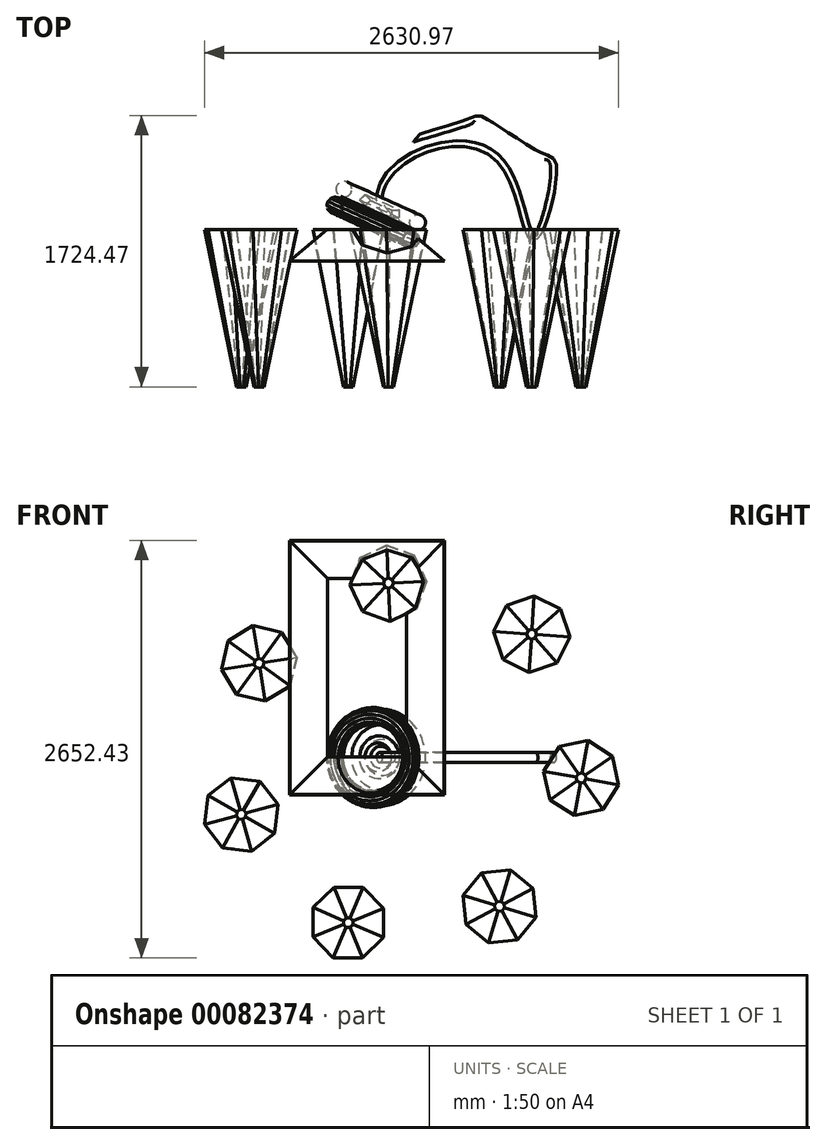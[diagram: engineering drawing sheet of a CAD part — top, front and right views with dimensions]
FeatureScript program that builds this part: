
annotation { "Feature Type Name" : "Feature", "Feature Type Description" : "" }
export const myFeature = defineFeature(function(context is Context, id is Id, definition is map)
    precondition{}
    {
        {
            var Q0;
            Q0=qCreatedBy(makeId("Top.planeOp"),FACE);
            var sketch = newSketch(context, id + "F0", { "sketchPlane" : qUnion([Q0])});
            skLineSegment(sketch, "E0.bottom", {"start": v(-50, 75) * mm, "end": v(-100, 75) * mm});
            skLineSegment(sketch, "E0.top", {"start": v(-50, 125) * mm, "end": v(-100, 125) * mm});
            skLineSegment(sketch, "E0.left", {"start": v(-50, 75) * mm, "end": v(-50, 125) * mm});
            skLineSegment(sketch, "E0.right", {"start": v(-100, 75) * mm, "end": v(-100, 125) * mm});
            skPoint(sketch, "E0.middle", {"position": v(-75, 100) * mm});
            skCircle(sketch, "E1", {"center": v(67, 45) * mm, "radius": 50 * mm});
            skArc(sketch, "E2", {"start": v(-125.25, -15.44) * mm, "mid": v(-116.96, -137.17) * mm, "end": v(-41.75, -41.1) * mm});
            skCircle(sketch, "E3.cCircle", {"center": v(25, -65) * mm, "radius": 52 * mm, "construction": true});
            skLineSegment(sketch, "E3.0", {"start": v(78, -57.37) * mm, "end": v(75.48, -82.88) * mm});
            skLineSegment(sketch, "E3.1", {"start": v(75.48, -82.88) * mm, "end": v(61.4, -104.3) * mm});
            skLineSegment(sketch, "E3.2", {"start": v(61.4, -104.3) * mm, "end": v(38.97, -116.7) * mm});
            skLineSegment(sketch, "E3.3", {"start": v(38.97, -116.7) * mm, "end": v(13.34, -117.27) * mm});
            skLineSegment(sketch, "E3.4", {"start": v(13.34, -117.27) * mm, "end": v(-9.62, -105.86) * mm});
            skLineSegment(sketch, "E3.5", {"start": v(-9.62, -105.86) * mm, "end": v(-24.64, -85.1) * mm});
            skLineSegment(sketch, "E3.6", {"start": v(-24.64, -85.1) * mm, "end": v(-28.3, -59.72) * mm});
            skLineSegment(sketch, "E3.7", {"start": v(-28.3, -59.72) * mm, "end": v(-19.74, -35.56) * mm});
            skLineSegment(sketch, "E3.8", {"start": v(-19.74, -35.56) * mm, "end": v(-0.93, -18.14) * mm});
            skLineSegment(sketch, "E3.9", {"start": v(-0.93, -18.14) * mm, "end": v(23.81, -11.46) * mm});
            skLineSegment(sketch, "E3.10", {"start": v(23.81, -11.46) * mm, "end": v(48.83, -17.04) * mm});
            skLineSegment(sketch, "E3.11", {"start": v(48.83, -17.04) * mm, "end": v(68.4, -33.6) * mm});
            skLineSegment(sketch, "E3.12", {"start": v(68.4, -33.6) * mm, "end": v(78, -57.37) * mm});
            skPoint(sketch, "E3.0.midPoint", {"position": v(76.75, -70.12) * mm});
            skLineSegment(sketch, "E4", {"start": v(-88.57, 324.23) * mm, "end": v(-325.42, -199.43) * mm});
            skSolve(sketch);
        }
        {
            var Q0;
            Q0=makeQuery(id+"F0.imprint","IMPRINT",FACE,{"disambiguationData":[TD([[makeQuery(id+"F0.imprint","IMPRINT",EDGE,{"derivedFrom":sQuery(id+"F0.wireOp",EDGE,"E0.bottom")}),-1.0]])]});
            var Q1;
            Q1=makeQuery(id+"F0.imprint","IMPRINT",FACE,{"disambiguationData":[TD([[makeQuery(id+"F0.imprint","IMPRINT",EDGE,{"derivedFrom":sQuery(id+"F0.wireOp",EDGE,"E1")}),1.0]])]});
            var Q2;
            Q2=makeQuery(id+"F0.imprint","IMPRINT",FACE,{"disambiguationData":[TD([[makeQuery(id+"F0.imprint","IMPRINT",EDGE,{"derivedFrom":sQuery(id+"F0.wireOp",EDGE,"E3.0")}),-1.0]])]});
            var Q3;
            Q3=sQuery(id+"F0.wireOp",EDGE,"E4");
            revolve(context, id + "F1", {"entities" : qUnion([Q0, Q1, Q2]), "axis" : qUnion([Q3]), "revolveType" : RevolveType.FULL});
        }
        {
            var Q0;
            Q0=qCreatedBy(makeId("Front.planeOp"),FACE);
            var sketch = newSketch(context, id + "F2", { "sketchPlane" : qUnion([Q0])});
            skCircle(sketch, "E5", {"center": v(0, 0) * mm, "radius": 32.69 * mm});
            skSolve(sketch);
        }
        {
            var Q0;
            Q0=qCreatedBy(makeId("Top.planeOp"),FACE);
            var sketch = newSketch(context, id + "F3", { "sketchPlane" : qUnion([Q0])});
            skFitSpline(sketch, "E6", {"points": [v(0, 0) * mm, v(-171.3, 185.68) * mm, v(20.92, 461.67) * mm, v(575.85, 453.64) * mm, v(784.46, -29.38) * mm, v(833.83, -20.36) * mm, v(926.7, 406.63) * mm, v(841.1, 473.01) * mm, v(470.96, 695.89) * mm, v(411.62, 690.18) * mm, v(61.2, 581.79) * mm], "startDerivative": vector(-2510.78, 1735.1) * mm, "endDerivative": vector(-3815.76, -1108.74) * mm});
            skSolve(sketch);
        }
        {
            var Q0;
            Q0=makeQuery(id+"F2.imprint","IMPRINT",FACE,{"disambiguationData":[TD([[makeQuery(id+"F2.imprint","IMPRINT",EDGE,{"derivedFrom":sQuery(id+"F2.wireOp",EDGE,"E5")}),1.0]])]});
            var Q1;
            Q1=sQuery(id+"F3.wireOp",EDGE,"E6");
            sweep(context, id + "F4", {"operationType" : NewBodyOperationType.ADD, "profiles" : qUnion([Q0]), "path" : qUnion([Q1])});
        }
        {
            var Q0;
            Q0=qCreatedBy(makeId("Front.planeOp"),FACE);
            var sketch = newSketch(context, id + "F5", { "sketchPlane" : qUnion([Q0])});
            skLineSegment(sketch, "E7.bottom", {"start": v(0, 0) * mm, "end": v(-509.4, 0) * mm});
            skLineSegment(sketch, "E7.top", {"start": v(0, 1140.13) * mm, "end": v(-509.4, 1140.13) * mm});
            skLineSegment(sketch, "E7.left", {"start": v(0, 0) * mm, "end": v(0, 1140.13) * mm});
            skLineSegment(sketch, "E7.right", {"start": v(-509.4, 0) * mm, "end": v(-509.4, 1140.13) * mm});
            skSolve(sketch);
        }
        {
            var Q0;
            Q0=makeQuery(id+"F5.imprint","IMPRINT",FACE,{"disambiguationData":[TD([[makeQuery(id+"F5.imprint","IMPRINT",EDGE,{"derivedFrom":sQuery(id+"F5.wireOp",EDGE,"E7.bottom")}),-1.0]])]});
            extrude(context, id + "F6", {"entities" : qUnion([Q0]), "depth" : 200 * mm, "hasDraft" : true, "draftAngle" : 50 * degree});
        }
        {
            var Q0;
            Q0=makeQuery(id+"F6.opExtrude","CAP_FACE",FACE,{"disambiguationData":[OSD([sQuery(id+"F5.wireOp",EDGE,"E7.bottom"),sQuery(id+"F5.wireOp",EDGE,"E7.top"),sQuery(id+"F5.wireOp",EDGE,"E7.left"),sQuery(id+"F5.wireOp",EDGE,"E7.right")])],"isStart":false});
            var Q1;
            Q1=makeQuery(id+"F6.opExtrude","CAP_FACE",FACE,{"disambiguationData":[OSD([sQuery(id+"F5.wireOp",EDGE,"E7.bottom"),sQuery(id+"F5.wireOp",EDGE,"E7.top"),sQuery(id+"F5.wireOp",EDGE,"E7.left"),sQuery(id+"F5.wireOp",EDGE,"E7.right")])],"isStart":true});
            shell(context, id + "F7", {"entities" : qUnion([Q0, Q1]), "thickness" : 2.5 * mm});
        }
        {
            var Q0;
            Q0=makeQuery(id+"F1.opRevolve","SWEPT_FACE",FACE,{"disambiguationData":[OSD([sQuery(id+"F0.wireOp",EDGE,"E3.2")])]});
            shell(context, id + "F8", {"entities" : qUnion([Q0]), "thickness" : 2.5 * mm});
        }
        {
            var Q0;
            Q0=qCreatedBy(makeId("Front.planeOp"),FACE);
            var sketch = newSketch(context, id + "F9", { "sketchPlane" : qUnion([Q0])});
            skCircle(sketch, "E8.cCircle", {"center": v(-939.52, 597.46) * mm, "radius": 224.04 * mm, "construction": true});
            skLineSegment(sketch, "E8.0", {"start": v(-901.5, 357.95) * mm, "end": v(-1082, 401.22) * mm});
            skLineSegment(sketch, "E8.1", {"start": v(-1082, 401.22) * mm, "end": v(-1179.02, 559.44) * mm});
            skLineSegment(sketch, "E8.2", {"start": v(-1179.02, 559.44) * mm, "end": v(-1135.76, 739.93) * mm});
            skLineSegment(sketch, "E8.3", {"start": v(-1135.76, 739.93) * mm, "end": v(-977.53, 836.96) * mm});
            skLineSegment(sketch, "E8.4", {"start": v(-977.53, 836.96) * mm, "end": v(-797.04, 793.7) * mm});
            skLineSegment(sketch, "E8.5", {"start": v(-797.04, 793.7) * mm, "end": v(-700.01, 635.48) * mm});
            skLineSegment(sketch, "E8.6", {"start": v(-700.01, 635.48) * mm, "end": v(-743.28, 454.98) * mm});
            skLineSegment(sketch, "E8.7", {"start": v(-743.28, 454.98) * mm, "end": v(-901.5, 357.95) * mm});
            skPoint(sketch, "E8.0.midPoint", {"position": v(-991.75, 379.59) * mm});
            skLineSegment(sketch, "E9.1.0", {"start": v(-1172.5, -573) * mm, "end": v(-1286.64, -426.63) * mm});
            skLineSegment(sketch, "E9.1.1", {"start": v(-1286.64, -426.63) * mm, "end": v(-1263.85, -242.43) * mm});
            skLineSegment(sketch, "E9.1.2", {"start": v(-1263.85, -242.43) * mm, "end": v(-1117.49, -128.3) * mm});
            skLineSegment(sketch, "E9.1.3", {"start": v(-1117.49, -128.3) * mm, "end": v(-933.29, -151.08) * mm});
            skLineSegment(sketch, "E9.1.4", {"start": v(-933.29, -151.08) * mm, "end": v(-819.15, -297.44) * mm});
            skLineSegment(sketch, "E9.1.5", {"start": v(-819.15, -297.44) * mm, "end": v(-841.94, -481.64) * mm});
            skPoint(sketch, "E9.1.6", {"position": v(-915.12, -538.71) * mm});
            skCircle(sketch, "E9.1.7", {"center": v(-1052.9, -362.04) * mm, "radius": 224.04 * mm, "construction": true});
            skLineSegment(sketch, "E9.1.8", {"start": v(-988.3, -595.78) * mm, "end": v(-1172.5, -573) * mm});
            skLineSegment(sketch, "E9.1.9", {"start": v(-841.94, -481.64) * mm, "end": v(-988.3, -595.78) * mm});
            skLineSegment(sketch, "E9.2.0", {"start": v(-283.06, -1273.95) * mm, "end": v(-468.65, -1271.93) * mm});
            skLineSegment(sketch, "E9.2.1", {"start": v(-468.65, -1271.93) * mm, "end": v(-598.46, -1139.27) * mm});
            skLineSegment(sketch, "E9.2.2", {"start": v(-598.46, -1139.27) * mm, "end": v(-596.44, -953.67) * mm});
            skLineSegment(sketch, "E9.2.3", {"start": v(-596.44, -953.67) * mm, "end": v(-463.78, -823.87) * mm});
            skLineSegment(sketch, "E9.2.4", {"start": v(-463.78, -823.87) * mm, "end": v(-278.18, -825.89) * mm});
            skLineSegment(sketch, "E9.2.5", {"start": v(-278.18, -825.89) * mm, "end": v(-148.38, -958.55) * mm});
            skPoint(sketch, "E9.2.6", {"position": v(-149.39, -1051.35) * mm});
            skCircle(sketch, "E9.2.7", {"center": v(-373.42, -1048.9) * mm, "radius": 224.04 * mm, "construction": true});
            skLineSegment(sketch, "E9.2.8", {"start": v(-150.4, -1144.15) * mm, "end": v(-283.06, -1273.95) * mm});
            skLineSegment(sketch, "E9.2.9", {"start": v(-148.38, -958.55) * mm, "end": v(-150.4, -1144.15) * mm});
            skLineSegment(sketch, "E9.3.0", {"start": v(819.53, -1015.6) * mm, "end": v(702.24, -1159.44) * mm});
            skLineSegment(sketch, "E9.3.1", {"start": v(702.24, -1159.44) * mm, "end": v(517.58, -1178.22) * mm});
            skLineSegment(sketch, "E9.3.2", {"start": v(517.58, -1178.22) * mm, "end": v(373.74, -1060.92) * mm});
            skLineSegment(sketch, "E9.3.3", {"start": v(373.74, -1060.92) * mm, "end": v(354.97, -876.27) * mm});
            skLineSegment(sketch, "E9.3.4", {"start": v(354.97, -876.27) * mm, "end": v(472.26, -732.42) * mm});
            skLineSegment(sketch, "E9.3.5", {"start": v(472.26, -732.42) * mm, "end": v(656.92, -713.65) * mm});
            skPoint(sketch, "E9.3.6", {"position": v(728.84, -772.3) * mm});
            skCircle(sketch, "E9.3.7", {"center": v(587.25, -945.93) * mm, "radius": 224.04 * mm, "construction": true});
            skLineSegment(sketch, "E9.3.8", {"start": v(800.76, -830.95) * mm, "end": v(819.53, -1015.6) * mm});
            skLineSegment(sketch, "E9.3.9", {"start": v(656.92, -713.65) * mm, "end": v(800.76, -830.95) * mm});
            skLineSegment(sketch, "E9.4.0", {"start": v(1305, 7.52) * mm, "end": v(1344.33, -173.87) * mm});
            skLineSegment(sketch, "E9.4.1", {"start": v(1344.33, -173.87) * mm, "end": v(1243.87, -329.94) * mm});
            skLineSegment(sketch, "E9.4.2", {"start": v(1243.87, -329.94) * mm, "end": v(1062.48, -369.27) * mm});
            skLineSegment(sketch, "E9.4.3", {"start": v(1062.48, -369.27) * mm, "end": v(906.41, -268.82) * mm});
            skLineSegment(sketch, "E9.4.4", {"start": v(906.41, -268.82) * mm, "end": v(867.08, -87.43) * mm});
            skLineSegment(sketch, "E9.4.5", {"start": v(867.08, -87.43) * mm, "end": v(967.53, 68.64) * mm});
            skPoint(sketch, "E9.4.6", {"position": v(1058.23, 88.3) * mm});
            skCircle(sketch, "E9.4.7", {"center": v(1105.7, -130.65) * mm, "radius": 224.04 * mm, "construction": true});
            skLineSegment(sketch, "E9.4.8", {"start": v(1148.92, 107.97) * mm, "end": v(1305, 7.52) * mm});
            skLineSegment(sketch, "E9.4.9", {"start": v(967.53, 68.64) * mm, "end": v(1148.92, 107.97) * mm});
            skLineSegment(sketch, "E9.5.0", {"start": v(807.77, 1024.98) * mm, "end": v(974.11, 942.63) * mm});
            skLineSegment(sketch, "E9.5.1", {"start": v(974.11, 942.63) * mm, "end": v(1033.5, 766.78) * mm});
            skLineSegment(sketch, "E9.5.2", {"start": v(1033.5, 766.78) * mm, "end": v(951.16, 600.45) * mm});
            skLineSegment(sketch, "E9.5.3", {"start": v(951.16, 600.45) * mm, "end": v(775.31, 541.05) * mm});
            skLineSegment(sketch, "E9.5.4", {"start": v(775.31, 541.05) * mm, "end": v(608.97, 623.4) * mm});
            skLineSegment(sketch, "E9.5.5", {"start": v(608.97, 623.4) * mm, "end": v(549.58, 799.25) * mm});
            skPoint(sketch, "E9.5.6", {"position": v(590.75, 882.42) * mm});
            skCircle(sketch, "E9.5.7", {"center": v(791.54, 783.02) * mm, "radius": 224.04 * mm, "construction": true});
            skLineSegment(sketch, "E9.5.8", {"start": v(631.93, 965.59) * mm, "end": v(807.77, 1024.98) * mm});
            skLineSegment(sketch, "E9.5.9", {"start": v(549.58, 799.25) * mm, "end": v(631.93, 965.59) * mm});
            skLineSegment(sketch, "E9.6.0", {"start": v(-297.72, 1270.6) * mm, "end": v(-129.63, 1349.31) * mm});
            skLineSegment(sketch, "E9.6.1", {"start": v(-129.63, 1349.31) * mm, "end": v(44.88, 1286.1) * mm});
            skLineSegment(sketch, "E9.6.2", {"start": v(44.88, 1286.1) * mm, "end": v(123.59, 1118.02) * mm});
            skLineSegment(sketch, "E9.6.3", {"start": v(123.59, 1118.02) * mm, "end": v(60.38, 943.5) * mm});
            skLineSegment(sketch, "E9.6.4", {"start": v(60.38, 943.5) * mm, "end": v(-107.7, 864.8) * mm});
            skLineSegment(sketch, "E9.6.5", {"start": v(-107.7, 864.8) * mm, "end": v(-282.22, 928) * mm});
            skPoint(sketch, "E9.6.6", {"position": v(-321.57, 1012.05) * mm});
            skCircle(sketch, "E9.6.7", {"center": v(-118.67, 1107.05) * mm, "radius": 224.04 * mm, "construction": true});
            skLineSegment(sketch, "E9.6.8", {"start": v(-360.92, 1096.1) * mm, "end": v(-297.72, 1270.6) * mm});
            skLineSegment(sketch, "E9.6.9", {"start": v(-282.22, 928) * mm, "end": v(-360.92, 1096.1) * mm});
            skPoint(sketch, "E9.center", {"position": v(0, 0) * mm});
            skSolve(sketch);
        }
        {
            var Q0;
            Q0=makeQuery(id+"F9.imprint","IMPRINT",FACE,{"disambiguationData":[TD([[makeQuery(id+"F9.imprint","IMPRINT",EDGE,{"derivedFrom":sQuery(id+"F9.wireOp",EDGE,"E9.5.0")}),-1.0]])]});
            var Q1;
            Q1=makeQuery(id+"F9.imprint","IMPRINT",FACE,{"disambiguationData":[TD([[makeQuery(id+"F9.imprint","IMPRINT",EDGE,{"derivedFrom":sQuery(id+"F9.wireOp",EDGE,"E9.4.0")}),-1.0]])]});
            var Q2;
            Q2=makeQuery(id+"F9.imprint","IMPRINT",FACE,{"disambiguationData":[TD([[makeQuery(id+"F9.imprint","IMPRINT",EDGE,{"derivedFrom":sQuery(id+"F9.wireOp",EDGE,"E9.3.0")}),-1.0]])]});
            var Q3;
            Q3=makeQuery(id+"F9.imprint","IMPRINT",FACE,{"disambiguationData":[TD([[makeQuery(id+"F9.imprint","IMPRINT",EDGE,{"derivedFrom":sQuery(id+"F9.wireOp",EDGE,"E9.2.0")}),-1.0]])]});
            var Q4;
            Q4=makeQuery(id+"F9.imprint","IMPRINT",FACE,{"disambiguationData":[TD([[makeQuery(id+"F9.imprint","IMPRINT",EDGE,{"derivedFrom":sQuery(id+"F9.wireOp",EDGE,"E9.1.0")}),-1.0]])]});
            var Q5;
            Q5=makeQuery(id+"F9.imprint","IMPRINT",FACE,{"disambiguationData":[TD([[makeQuery(id+"F9.imprint","IMPRINT",EDGE,{"derivedFrom":sQuery(id+"F9.wireOp",EDGE,"E8.0")}),-1.0]])]});
            var Q6;
            Q6=makeQuery(id+"F9.imprint","IMPRINT",FACE,{"disambiguationData":[TD([[makeQuery(id+"F9.imprint","IMPRINT",EDGE,{"derivedFrom":sQuery(id+"F9.wireOp",EDGE,"E9.6.0")}),-1.0]])]});
            extrude(context, id + "F10", {"entities" : qUnion([Q0, Q1, Q2, Q3, Q4, Q5, Q6]), "operationType" : NewBodyOperationType.ADD, "depth" : 1000 * mm, "hasDraft" : true, "draftAngle" : 11 * degree, "draftPullDirection" : true});
        }
        {
            var Q0;
            Q0=makeQuery(id+"F10.opExtrude","CAP_FACE",FACE,{"disambiguationData":[OSD([sQuery(id+"F9.wireOp",EDGE,"E9.1.0"),sQuery(id+"F9.wireOp",EDGE,"E9.1.1"),sQuery(id+"F9.wireOp",EDGE,"E9.1.2"),sQuery(id+"F9.wireOp",EDGE,"E9.1.3"),sQuery(id+"F9.wireOp",EDGE,"E9.1.4"),sQuery(id+"F9.wireOp",EDGE,"E9.1.5"),sQuery(id+"F9.wireOp",EDGE,"E9.1.8"),sQuery(id+"F9.wireOp",EDGE,"E9.1.9")])],"isStart":true});
            var Q1;
            Q1=makeQuery(id+"F10.opExtrude","CAP_FACE",FACE,{"disambiguationData":[OSD([sQuery(id+"F9.wireOp",EDGE,"E8.0"),sQuery(id+"F9.wireOp",EDGE,"E8.1"),sQuery(id+"F9.wireOp",EDGE,"E8.2"),sQuery(id+"F9.wireOp",EDGE,"E8.3"),sQuery(id+"F9.wireOp",EDGE,"E8.4"),sQuery(id+"F9.wireOp",EDGE,"E8.5"),sQuery(id+"F9.wireOp",EDGE,"E8.6"),sQuery(id+"F9.wireOp",EDGE,"E8.7")])],"isStart":true});
            var Q2;
            Q2=makeQuery(id+"F10.boolean.opBoolean","MERGE",FACE,{"derivedFrom":[makeQuery(id+"F6.opExtrude","CAP_FACE",FACE,{"disambiguationData":[OSD([sQuery(id+"F5.wireOp",EDGE,"E7.bottom"),sQuery(id+"F5.wireOp",EDGE,"E7.top"),sQuery(id+"F5.wireOp",EDGE,"E7.left"),sQuery(id+"F5.wireOp",EDGE,"E7.right")])],"isStart":true}),makeQuery(id+"F10.opExtrude","CAP_FACE",FACE,{"disambiguationData":[OSD([sQuery(id+"F9.wireOp",EDGE,"E9.6.0"),sQuery(id+"F9.wireOp",EDGE,"E9.6.1"),sQuery(id+"F9.wireOp",EDGE,"E9.6.2"),sQuery(id+"F9.wireOp",EDGE,"E9.6.3"),sQuery(id+"F9.wireOp",EDGE,"E9.6.4"),sQuery(id+"F9.wireOp",EDGE,"E9.6.5"),sQuery(id+"F9.wireOp",EDGE,"E9.6.8"),sQuery(id+"F9.wireOp",EDGE,"E9.6.9")])],"isStart":true})]});
            var Q3;
            Q3=makeQuery(id+"F10.opExtrude","CAP_FACE",FACE,{"disambiguationData":[OSD([sQuery(id+"F9.wireOp",EDGE,"E9.5.0"),sQuery(id+"F9.wireOp",EDGE,"E9.5.1"),sQuery(id+"F9.wireOp",EDGE,"E9.5.2"),sQuery(id+"F9.wireOp",EDGE,"E9.5.3"),sQuery(id+"F9.wireOp",EDGE,"E9.5.4"),sQuery(id+"F9.wireOp",EDGE,"E9.5.5"),sQuery(id+"F9.wireOp",EDGE,"E9.5.8"),sQuery(id+"F9.wireOp",EDGE,"E9.5.9")])],"isStart":true});
            var Q4;
            Q4=makeQuery(id+"F10.opExtrude","CAP_FACE",FACE,{"disambiguationData":[OSD([sQuery(id+"F9.wireOp",EDGE,"E9.4.0"),sQuery(id+"F9.wireOp",EDGE,"E9.4.1"),sQuery(id+"F9.wireOp",EDGE,"E9.4.2"),sQuery(id+"F9.wireOp",EDGE,"E9.4.3"),sQuery(id+"F9.wireOp",EDGE,"E9.4.4"),sQuery(id+"F9.wireOp",EDGE,"E9.4.5"),sQuery(id+"F9.wireOp",EDGE,"E9.4.8"),sQuery(id+"F9.wireOp",EDGE,"E9.4.9")])],"isStart":true});
            var Q5;
            Q5=makeQuery(id+"F10.opExtrude","CAP_FACE",FACE,{"disambiguationData":[OSD([sQuery(id+"F9.wireOp",EDGE,"E9.3.0"),sQuery(id+"F9.wireOp",EDGE,"E9.3.1"),sQuery(id+"F9.wireOp",EDGE,"E9.3.2"),sQuery(id+"F9.wireOp",EDGE,"E9.3.3"),sQuery(id+"F9.wireOp",EDGE,"E9.3.4"),sQuery(id+"F9.wireOp",EDGE,"E9.3.5"),sQuery(id+"F9.wireOp",EDGE,"E9.3.8"),sQuery(id+"F9.wireOp",EDGE,"E9.3.9")])],"isStart":true});
            var Q6;
            Q6=makeQuery(id+"F10.opExtrude","CAP_FACE",FACE,{"disambiguationData":[OSD([sQuery(id+"F9.wireOp",EDGE,"E9.2.0"),sQuery(id+"F9.wireOp",EDGE,"E9.2.1"),sQuery(id+"F9.wireOp",EDGE,"E9.2.2"),sQuery(id+"F9.wireOp",EDGE,"E9.2.3"),sQuery(id+"F9.wireOp",EDGE,"E9.2.4"),sQuery(id+"F9.wireOp",EDGE,"E9.2.5"),sQuery(id+"F9.wireOp",EDGE,"E9.2.8"),sQuery(id+"F9.wireOp",EDGE,"E9.2.9")])],"isStart":true});
            shell(context, id + "F11", {"entities" : qUnion([Q0, Q1, Q2, Q3, Q4, Q5, Q6]), "thickness" : 2.5 * mm});
        }
    });
